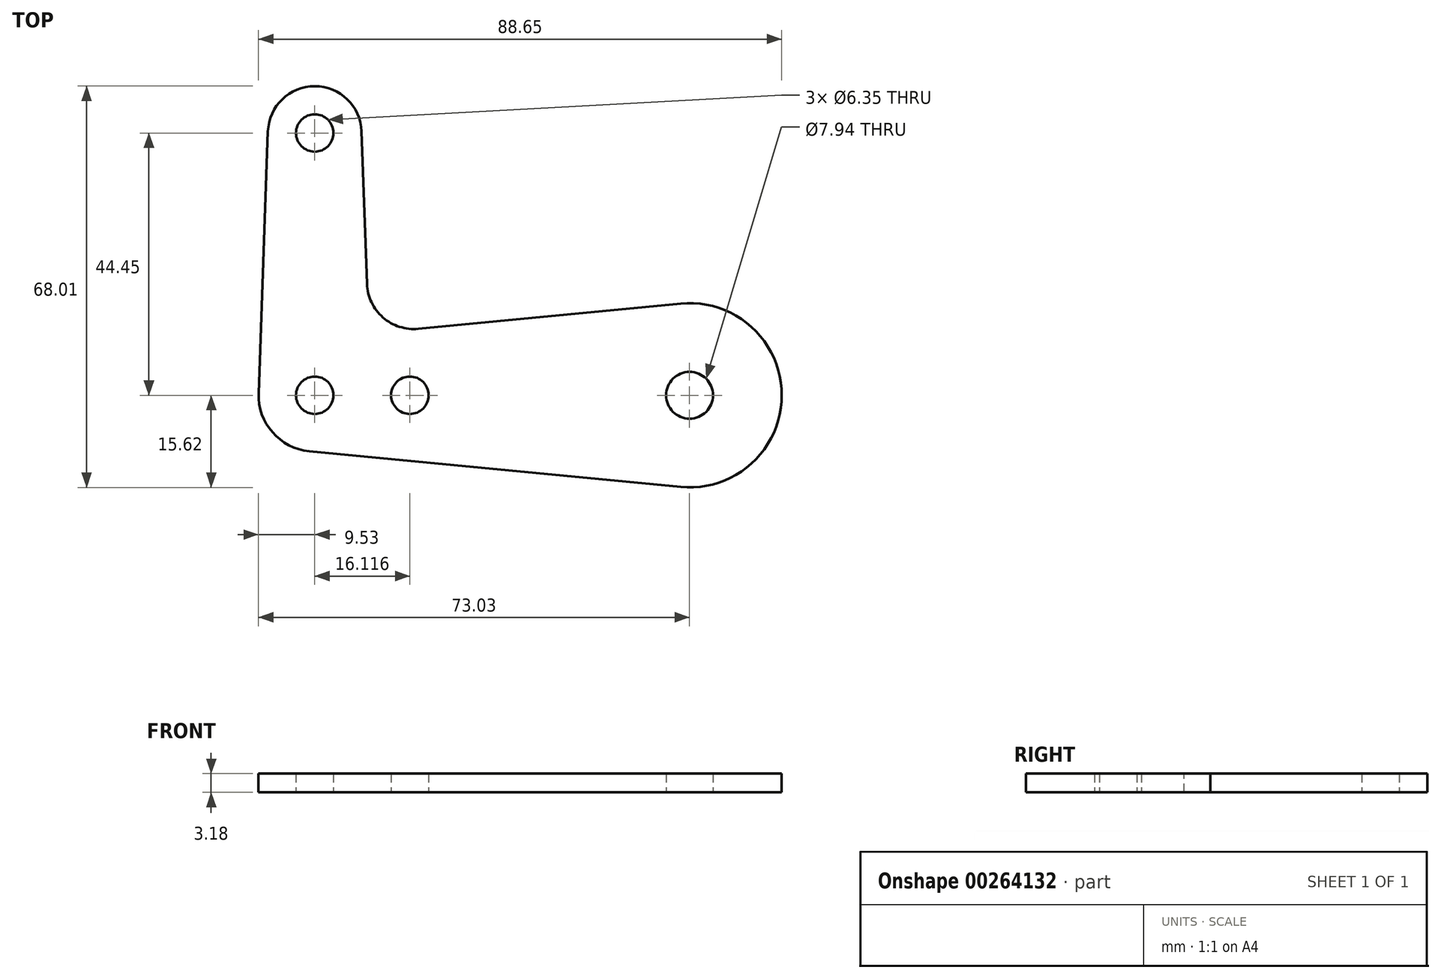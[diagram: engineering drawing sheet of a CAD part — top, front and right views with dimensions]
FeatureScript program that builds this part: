
annotation { "Feature Type Name" : "Feature", "Feature Type Description" : "" }
export const myFeature = defineFeature(function(context is Context, id is Id, definition is map)
    precondition{}
    {
        {
            var Q0;
            Q0=qCreatedBy(makeId("Top.planeOp"),FACE);
            var sketch = newSketch(context, id + "F0", { "sketchPlane" : qUnion([Q0])});
            skLineSegment(sketch, "E0", {"start": v(0, 0) * mm, "end": v(63.5, 0) * mm, "construction": true});
            skLineSegment(sketch, "E1", {"start": v(0, 0) * mm, "end": v(0, 44.45) * mm, "construction": true});
            skCircle(sketch, "E2", {"center": v(0, 44.45) * mm, "radius": 7.94 * mm});
            skCircle(sketch, "E3", {"center": v(0, 0) * mm, "radius": 9.53 * mm});
            skCircle(sketch, "E4", {"center": v(63.5, 0) * mm, "radius": 15.62 * mm});
            skCircle(sketch, "E5", {"center": v(0, 44.45) * mm, "radius": 3.18 * mm});
            skCircle(sketch, "E6", {"center": v(0, 0) * mm, "radius": 3.18 * mm});
            skCircle(sketch, "E7", {"center": v(63.5, 0) * mm, "radius": 3.97 * mm});
            skLineSegment(sketch, "E8", {"start": v(-0.91, -9.48) * mm, "end": v(62, -15.55) * mm});
            skLineSegment(sketch, "E9", {"start": v(-0.91, 9.48) * mm, "end": v(62, 15.55) * mm});
            skLineSegment(sketch, "E10", {"start": v(7.93, 44.73) * mm, "end": v(9.53, 0) * mm});
            skLineSegment(sketch, "E11", {"start": v(-7.93, 44.73) * mm, "end": v(-9.52, 0.34) * mm});
            skCircle(sketch, "E12", {"center": v(16.12, 0) * mm, "radius": 3.18 * mm});
            skSolve(sketch);
        }
        {
            var Q0;
            Q0 = qSketchRegion(id + "F0", true);
            var Q1;
            {var subQ4=sQuery(id+"F0.wireOp",EDGE,"E6");var subQ6=sQuery(id+"F0.wireOp",EDGE,"E0");var subQ8=makeQuery(id+"F0.imprint","INTERSECT",VERTEX,{"derivedFrom":[subQ6,subQ4]});Q1=makeQuery(id+"F0.imprint","IMPRINT",FACE,{"disambiguationData":[TD([[makeQuery(id+"F0.imprint","IMPRINT",EDGE,{"disambiguationData":[TD([[subQ8,-1.0]])],"derivedFrom":subQ6}),1.0]])]});}
            extrude(context, id + "F1", {"entities" : qUnion([Q0, Q1]), "depth" : 3.17 * mm});
        }
        {
            var Q0;
            Q0=makeQuery(id+"F1.opExtrude","SWEPT_EDGE",EDGE,{"disambiguationData":[OSD([sQuery(id+"F0.wireOp",EDGE,"E9"),sQuery(id+"F0.wireOp",EDGE,"E10")])]});
            fillet(context, id + "F2", {"entities" : qUnion([Q0]), "radius" : 7.94 * mm, "tangentPropagation" : true, "allowEdgeOverflow" : false});
        }
    });
